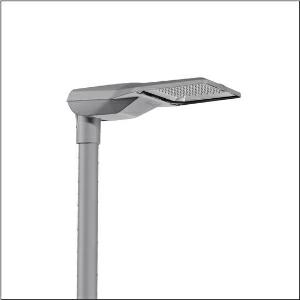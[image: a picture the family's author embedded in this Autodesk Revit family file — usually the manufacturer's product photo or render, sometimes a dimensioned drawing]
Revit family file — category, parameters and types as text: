
# Revit family: streetlight_sl_21_iq_midi___st0_5a_5xe3b31g08nb_5b56
name_source: partatom
category: Lighting Fixtures
units: mm (PartAtom-declared; Revit-internal decimal feet)

## family parameters
Cut with Voids When Loaded = No
Host = Face
Light Source = No
Part Type = Normal
Room Calculation Point = No
Round Connector Dimension = Use Diameter
Shared = No

## types (1)
- --- (1 x LED, 23230 lm, 155.5 W, 3000K)
    Apparent Load = 155 VA
    CIE Flux Codes = 43 76 97 100 100
    Color Rendering = 70
    Color Temperature = 3000K
    Default Elevation = 1800 mm
    Description = Streetlight SL 21 iQ midi, mast luminaire, primary light control with lens, of PMMA, primary optical cover: cover, of toughened safety glass, transparent, light distribution: ST0.5a, light emission: direct distribution, primary light characteristic: asymmetric, installation type: post-top, side-entry, LED, High Power LED, rated luminous flux: 23.230lm, luminous efficacy: 149lm/W, light colour: 730, colour temperature: 3000K, control: Street-Remote, Auto-Match, Temp-Guard, Lumen-Switch, Night-Set, Smart-Wire, Light-Fading, Desk-Remote (wireless, voltage-free reading and setting of iQ features in the workshop via application-optimized NFC function/RFID function), optimised constant luminous flux control (CLO 2.0), presetting dimming linear, mains connection: 230..240V, AC, 50/60Hz, start of lifetime: 156W, end of service life: 162W, reduction: 69W, luminaire housing, of diecast aluminium, powder-coated, Siteco® metallic grey (DB 702S), corrosivity category C5 mid according to DIN EN ISO 12944, please order mast flange separately, inclination adjustable: 0°, 5°, 10°, 15°, sealing non-destructively replaceable, multi-level sealing system, length: 644mm, width: 335mm, height: 110mm, mast flange for spigot size: 42mm (side-entry): 5XC10008XM4, 60/48mm (side-entry/post-top): 5XC10108XM2, 76/60mm (side-entry/post-top): 5XC10108XM1, protection rating (complete): IP66, insulation class (complete): insulation class II (safety insulation), certification: CE, ENEC, ENEC+, VDE, impact resistance: IK09, permissible operating ambient temperature for outdoor applications: -40..+50°C, standard-compliant lighting for roads and squares, packaging unit: 1 piece

Light Distribution: ST0.5a
    Height = 111 mm
    Lamp = 1 x LED
    Lamp Light Flux = 23230 lm
    Lamp Power = 155.5 W
    Lamp count = 1
    Length = 644 mm
    Luminous efficacy = 149 lm/W
    Manufacturer = Siteco
    ModVariant = No
    Model = 5XE3B31G08NB
    Number of Poles = 1
    OnlyDefault = Yes
    Power Factor = 1
    Product Name = Streetlight SL 21 iQ midi | ST0.5a
    Product group = mast luminaire | pylon top
    ProductGroupID = 6100
    Protection Class = Protection class II
    Protection Degree = IP 66
    RLX_Detail_Level = 1
    RLX_Emergency_Light_Flux = 0 lm
    RLX_Emergency_Type = 0
    RLX_Emergency_Type_DB = No
    RlxData = <blob elided: 102253 chars, md5=fcee266d>
    Socket = socket
    Standby Power = 0 W
    System Light Flux = 23230 lm
    System Power = 155 W
    Type Comments = factory setting: luminous flux: 100 % | dim-lin: 254 | 823 mA
    Type Image = l_1004298.jpg
    URL = http://relux.com
    VarID = @adj_104469
    Voltage = 0 V
    Weight = 0.00 kg
    Width = 336 mm

## geometry (parser evidence)
native form markers: Blend x4, Sweep x9
no freeform markers — native parametric forms only
